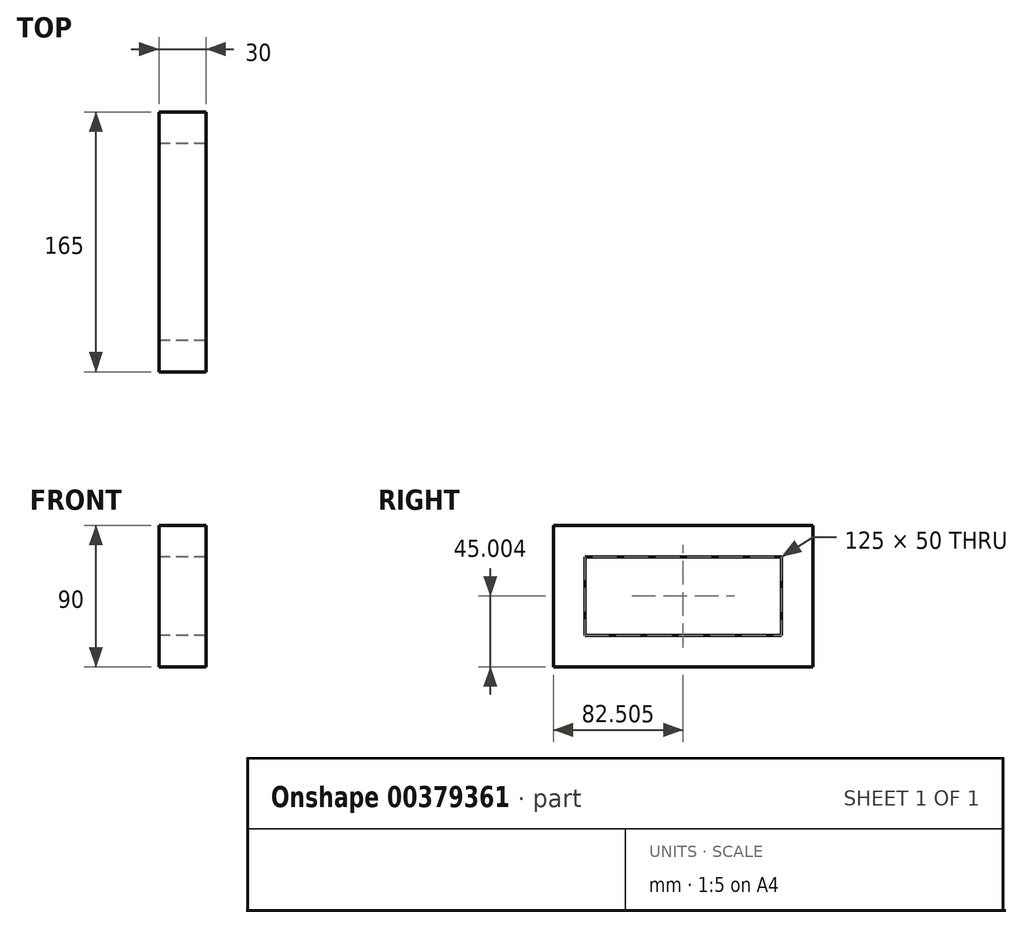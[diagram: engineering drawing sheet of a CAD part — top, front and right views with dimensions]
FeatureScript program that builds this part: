
annotation { "Feature Type Name" : "Feature", "Feature Type Description" : "" }
export const myFeature = defineFeature(function(context is Context, id is Id, definition is map)
    precondition{}
    {
        {
            var Q0;
            Q0=qCreatedBy(makeId("Right.planeOp"),FACE);
            var sketch = newSketch(context, id + "F0", { "sketchPlane" : qUnion([Q0])});
            skLineSegment(sketch, "E0.bottom", {"start": v(-76.08, 73.26) * mm, "end": v(88.92, 73.26) * mm});
            skLineSegment(sketch, "E0.top", {"start": v(-76.08, -16.74) * mm, "end": v(88.92, -16.74) * mm});
            skLineSegment(sketch, "E0.left", {"start": v(-76.08, 73.26) * mm, "end": v(-76.08, -16.74) * mm});
            skLineSegment(sketch, "E0.right", {"start": v(88.92, 73.26) * mm, "end": v(88.92, -16.74) * mm});
            skLineSegment(sketch, "E1.bottom", {"start": v(-56.08, 53.26) * mm, "end": v(68.92, 53.26) * mm});
            skLineSegment(sketch, "E1.top", {"start": v(-56.08, 3.26) * mm, "end": v(68.92, 3.26) * mm});
            skLineSegment(sketch, "E1.left", {"start": v(-56.08, 53.26) * mm, "end": v(-56.08, 3.26) * mm});
            skLineSegment(sketch, "E1.right", {"start": v(68.92, 53.26) * mm, "end": v(68.92, 3.26) * mm});
            skSolve(sketch);
        }
        {
            var Q0;
            Q0=makeQuery(id+"F0.imprint","IMPRINT",FACE,{"disambiguationData":[TD([[makeQuery(id+"F0.imprint","IMPRINT",EDGE,{"derivedFrom":sQuery(id+"F0.wireOp",EDGE,"E0.bottom")}),-1.0]])]});
            extrude(context, id + "F1", {"entities" : qUnion([Q0]), "depth" : 30 * mm, "offsetDistance" : 25 * mm});
        }
    });
